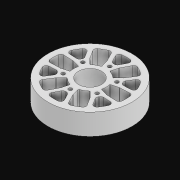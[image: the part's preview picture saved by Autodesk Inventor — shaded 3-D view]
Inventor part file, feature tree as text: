
AUTODESK INVENTOR PART (.ipt)
format: ipt  version: 2021 (Build 250183000, 183)  size: 576,000 bytes
history: native  units: in
note: dims shown in document units (in); Inventor stores cm internally (conversion verified against a paired STEP export)
features: other x10, extrude x2, sketch x2, projected_geometry x2, pattern_circular x1
ambient origin geometry x8: Origin, YZ Plane, XZ Plane, XY Plane, X Axis, Y Axis, Z Axis, Center Point
bodies: Solid1 (feature_tree)
feature tree (17):
  other  "Table"
  other  "Thickness = 1.000 in"
  other  "Color = 60a Flex Wheel"
  other  "Color = 30a Flex Wheel"
  other  "Color = 40a Flex Wheel"
  other  "Thickness = 0.375 in"
  other  "Thickness = 0.500 in"
  other  "Thickness = 0.125 in"
  other  "Thickness = 0.750 in"
  other  "Thickness = 0.250 in"
  pattern_circular  "CirPattern2"
  extrude  "Extrusion1"  Depth=1.0in TaperAngle=0.0deg
  extrude  "Extrusion2"  [1 undecoded]
  sketch  "Sketch1"  dims[d1=0.0in d2=1.0in d3=0.0in]
  projected_geometry  "Projected Loop1"
  sketch  "Sketch2"
  projected_geometry  "Projected Loop2"
note: 1 required parameter value undecoded (feature->parameter linkage not recoverable at this tier; creation-order binding heuristic only, values carry confidence <= 0.55)
